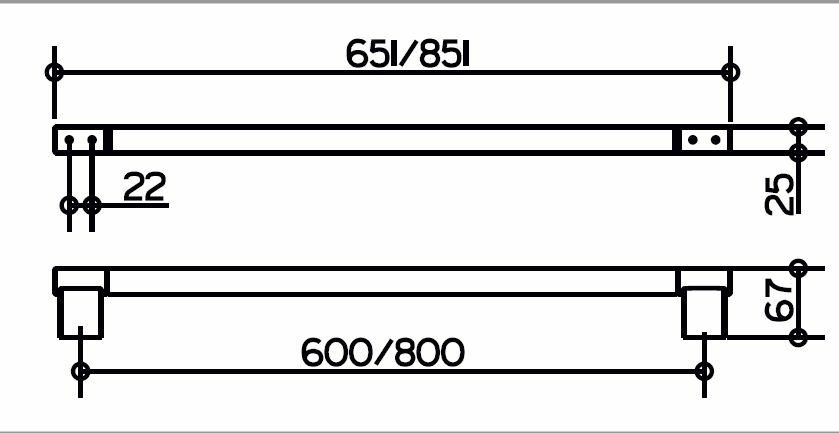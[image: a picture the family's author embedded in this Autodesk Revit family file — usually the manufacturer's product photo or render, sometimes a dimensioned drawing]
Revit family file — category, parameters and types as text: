
# Revit family: KEUCO_34981010037
name_source: partatom
category: Allgemeines Modell
revit_build: Autodesk Revit 2016 (Build: 20150220_1215(x64)
units: mm (PartAtom-declared; Revit-internal decimal feet)

## family parameters
Arbeitsebenenbasiert = Ja
Beim Laden mit Abzugskörper schneiden = Nein
Bemaßung runder Anschluss = Durchmesser verwenden
Gemeinsam genutzt = Nein
Immer vertikal = Nein
Kann Basisbauteil für Bewehrung sein = Nein
Raumberechnungspunkt = Nein
Teiletyp = Normal

## types (6) — shared parameters
Beschreibung = zum Einhängen in Haltegriffe
sowie Dusch- und Wannenhandläufe,
Sitzfläche nach oben klappbar,
Rückenlehne abnehmbar
Hersteller = KEUCO
Serie = Plan
URL = https://www.keuco.com
Verwendung = CA / DU
Vorgabe-Ansicht = 1219 mm
zero-valued in all types: Gewicht

## per-type parameters (varying)
| type | Ausschreibungstext | Material | Material Stahl |
| 34981010037 | KEUCO PLAN CARE Klappsitz 34981010037
schwarzgrauer (RAL 7021) Klappsitz 
aus Polypropylen 
in ästhetischem, funktionalem Design, 
zum Einhängen in Haltegriffe und Duschhandläufe
für sicheres Sitzen im Duschbereich,
Sitzträger als Design-Element hochglanzverchromt,
antistatisch, leichte Reinigung,
Materialschonende Aufhängung 
durch integrierte Kunststoffschalen 
zum Haltegriff / Handlauf 
und Kunststoffpuffer zur Wandfliese,
nach oben klappbarer Sitz belastbar bis 110 kg,
Breite 362 mm, Länge der Sitzfläche 310 mm
Ausladung 489 mm

Zur Komplettierung des Artikels unbedingt
erforderlich:
Artikel aus dem Stangensystem Plan Care
(Artikel-Nr. 34901 - 34915) | Schwarzgrau | Stahl, verchromt |
| 34981010038 | KEUCO PLAN CARE Klappsitz 34981010038
lichtgrauer (RAL 7035) Klappsitz 
aus Polypropylen 
in ästhetischem, funktionalem Design, 
zum Einhängen in Haltegriffe und Duschhandläufe
für sicheres Sitzen im Duschbereich,
Sitzträger als Design-Element hochglanzverchromt,
antistatisch, leichte Reinigung,
Materialschonende Aufhängung 
durch integrierte Kunststoffschalen 
zum Haltegriff / Handlauf 
und Kunststoffpuffer zur Wandfliese,
nach oben klappbarer Sitz belastbar bis 110 kg,
Breite 362 mm, Länge der Sitzfläche 310 mm
Ausladung 489 mm

Zur Komplettierung des Artikels unbedingt
erforderlich:
Artikel aus dem Stangensystem Plan Care
(Artikel-Nr. 34901 - 34915) | Lichtgrau (RAL 7035) | Stahl, verchromt |
| 34981010051 | KEUCO PLAN CARE Klappsitz 34981010051
weißer (RAL 9010) Klappsitz 
aus Polypropylen 
in ästhetischem, funktionalem Design, 
zum Einhängen in Haltegriffe und Duschhandläufe
für sicheres Sitzen im Duschbereich,
Sitzträger als Design-Element hochglanzverchromt,
antistatisch, leichte Reinigung,
Materialschonende Aufhängung 
durch integrierte Kunststoffschalen 
zum Haltegriff / Handlauf 
und Kunststoffpuffer zur Wandfliese,
nach oben klappbarer Sitz belastbar bis 110 kg,
Breite 362 mm, Länge der Sitzfläche 310 mm
Ausladung 489 mm

Zur Komplettierung des Artikels unbedingt
erforderlich:
Artikel aus dem Stangensystem Plan Care
(Artikel-Nr. 34901 - 34915) | Weiß (RAL 9010) | Stahl, verchromt |
| 34981170037 | KEUCO PLAN CARE Klappsitz 34981170037
schwarzgrauer (RAL 7021) Klappsitz 
aus Polypropylen 
in ästhetischem, funktionalem Design, 
zum Einhängen in Haltegriffe und Duschhandläufe
für sicheres Sitzen im Duschbereich,
Sitzträger als Design-Element aus
silber-eloxiertem Aluminium (E6 EV1),
antistatisch, leichte Reinigung,
materialschonende Aufhängung 
durch integrierte Kunststoffschalen 
zum Haltegriff / Handlauf 
und Kunststoffpuffer zur Wandfliese,
nach oben klappbarer Sitz belastbar bis 110 kg,
Breite 362 mm, Länge der Sitzfläche 310 mm
Ausladung 489 mm

Zur Komplettierung des Artikels unbedingt
erforderlich:
Artikel aus dem Stangensystem Plan Care
(Artikel-Nr. 34901 - 34915) | Schwarzgrau | Aluminium 1100-H18 |
| 34981170038 | KEUCO PLAN CARE Klappsitz 34981170038
lichtgrauer (RAL 7035) Klappsitz 
aus Polypropylen 
in ästhetischem, funktionalem Design, 
zum Einhängen in Haltegriffe und Duschhandläufe
für sicheres Sitzen im Duschbereich,
Sitzträger als Design-Element aus
silber-eloxiertem Aluminium (E6 EV1),
antistatisch, leichte Reinigung,
materialschonende Aufhängung 
durch integrierte Kunststoffschalen 
zum Haltegriff / Handlauf 
und Kunststoffpuffer zur Wandfliese,
nach oben klappbarer Sitz belastbar bis 110 kg,
Breite 362 mm, Länge der Sitzfläche 310 mm
Ausladung 489 mm

Zur Komplettierung des Artikels unbedingt
erforderlich:
Artikel aus dem Stangensystem Plan Care
(Artikel-Nr. 34901 - 34915) | Lichtgrau (RAL 7035) | Aluminium 1100-H18 |
| 34981170051 | KEUCO PLAN CARE Klappsitz 34981170051
weißer (RAL 9010) Klappsitz 
aus Polypropylen 
in ästhetischem, funktionalem Design, 
zum Einhängen in Haltegriffe und Duschhandläufe
für sicheres Sitzen im Duschbereich,
Sitzträger als Design-Element aus
silber-eloxiertem Aluminium (E6 EV1),
antistatisch, leichte Reinigung,
materialschonende Aufhängung 
durch integrierte Kunststoffschalen 
zum Haltegriff / Handlauf 
und Kunststoffpuffer zur Wandfliese,
nach oben klappbarer Sitz belastbar bis 110 kg,
Breite 362 mm, Länge der Sitzfläche 310 mm
Ausladung 489 mm

Zur Komplettierung des Artikels unbedingt
erforderlich:
Artikel aus dem Stangensystem Plan Care
(Artikel-Nr. 34901 - 34915) | Schwarzgrau | Aluminium 1100-H18 |

note: column(s) folded — value = type name in every type: Artikelnummer

## geometry (parser evidence)
native form markers: Blend x2, Sweep x2
no freeform markers — native parametric forms only
